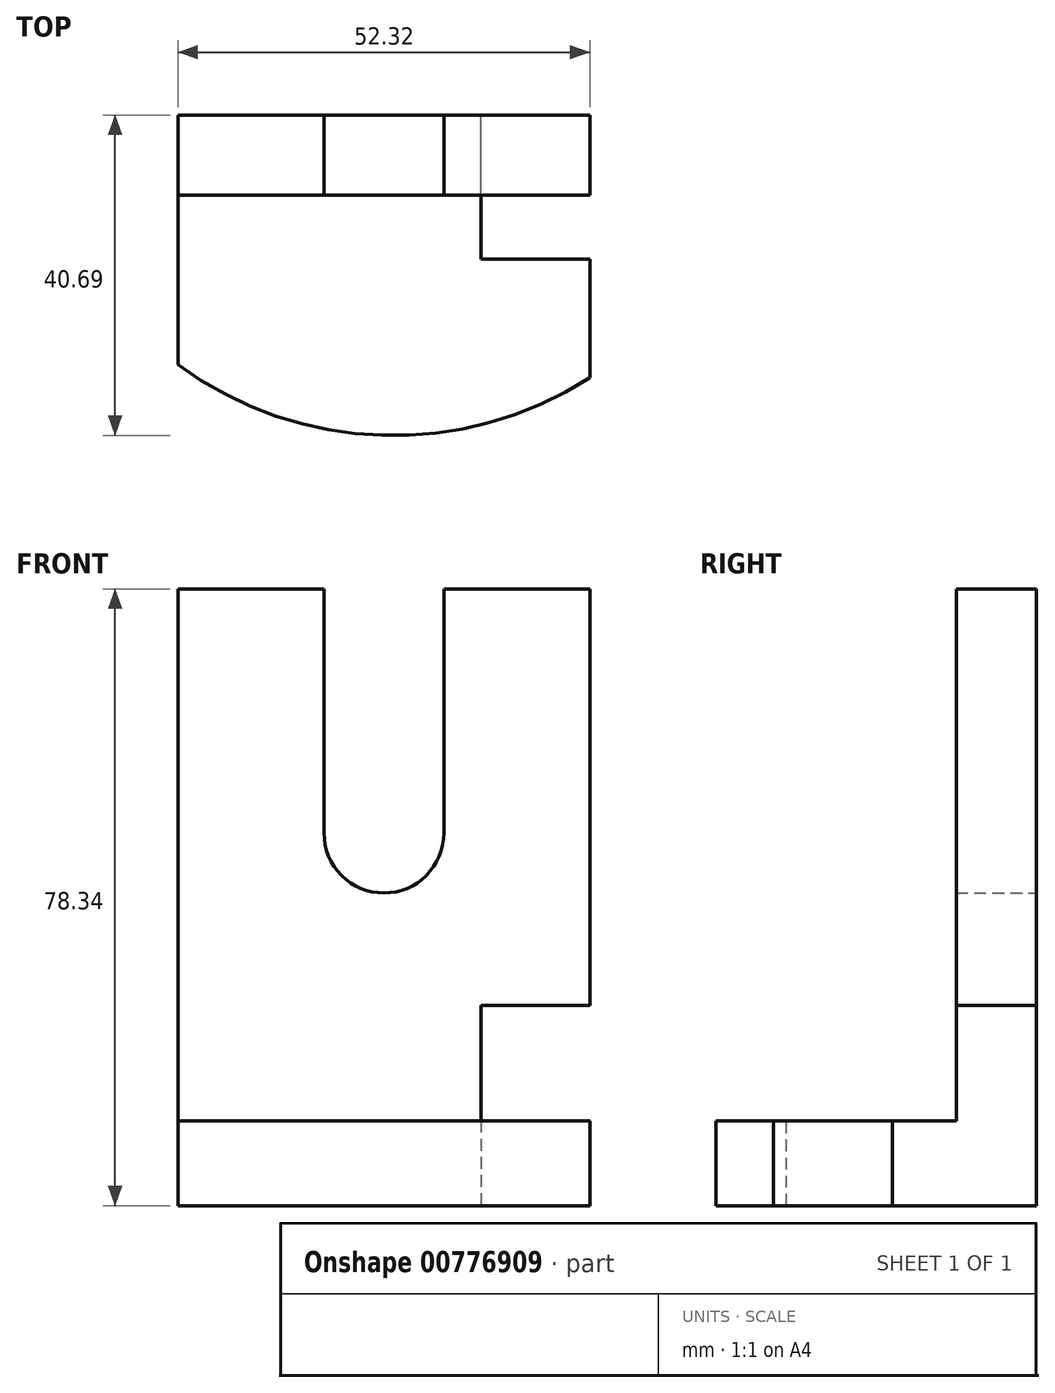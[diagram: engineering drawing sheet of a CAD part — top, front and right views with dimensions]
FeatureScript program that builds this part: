
annotation { "Feature Type Name" : "Feature", "Feature Type Description" : "" }
export const myFeature = defineFeature(function(context is Context, id is Id, definition is map)
    precondition{}
    {
        {
            var Q0;
            Q0=qCreatedBy(makeId("Front.planeOp"),FACE);
            var sketch = newSketch(context, id + "F0", { "sketchPlane" : qUnion([Q0])});
            skLineSegment(sketch, "E0.bottom", {"start": v(26.16, 39.17) * mm, "end": v(7.61, 39.17) * mm});
            skLineSegment(sketch, "E0.top", {"start": v(26.16, -39.17) * mm, "end": v(-26.16, -39.17) * mm});
            skLineSegment(sketch, "E0.left", {"start": v(26.16, 39.17) * mm, "end": v(26.16, -39.17) * mm});
            skLineSegment(sketch, "E0.right", {"start": v(-26.16, 39.17) * mm, "end": v(-26.16, -39.17) * mm});
            skPoint(sketch, "E0.middle", {"position": v(0, 0) * mm});
            skLineSegment(sketch, "E1.left", {"start": v(7.61, 39.17) * mm, "end": v(7.61, 8.16) * mm});
            skLineSegment(sketch, "E1.right", {"start": v(-7.61, 39.17) * mm, "end": v(-7.61, 8.16) * mm});
            skPoint(sketch, "E1.middle", {"position": v(0, 23.67) * mm});
            skLineSegment(sketch, "E2", {"start": v(-26.16, -28.38) * mm, "end": v(26.16, -28.38) * mm});
            skLineSegment(sketch, "E3.trimOffspring", {"start": v(-7.61, 39.17) * mm, "end": v(-26.16, 39.17) * mm});
            skArc(sketch, "E4", {"start": v(-7.61, 8.16) * mm, "mid": v(0, 0.55) * mm, "end": v(7.61, 8.16) * mm});
            skSolve(sketch);
        }
        {
            var Q0;
            {var subQ4=sQuery(id+"F0.wireOp",EDGE,"E0.bottom");Q0=makeQuery(id+"F0.imprint","IMPRINT",FACE,{"disambiguationData":[TD([[makeQuery(id+"F0.imprint","IMPRINT",EDGE,{"derivedFrom":subQ4}),1.0]])]});}
            extrude(context, id + "F1", {"entities" : qUnion([Q0]), "depth" : 10.16 * mm, "offsetDistance" : 25.4 * mm});
        }
        {
            var Q0;
            {var subQ0=sQuery(id+"F0.wireOp",EDGE,"E0.top");Q0=makeQuery(id+"F0.imprint","IMPRINT",FACE,{"disambiguationData":[TD([[makeQuery(id+"F0.imprint","IMPRINT",EDGE,{"derivedFrom":subQ0}),-1.0]])]});}
            extrude(context, id + "F2", {"entities" : qUnion([Q0]), "operationType" : NewBodyOperationType.ADD, "depth" : 45.2 * mm, "offsetDistance" : 25.4 * mm});
        }
        {
            var Q0;
            Q0=makeQuery(id+"F2.opExtrude","SWEPT_FACE",FACE,{"disambiguationData":[OSD([sQuery(id+"F0.wireOp",EDGE,"E2")])]});
            var sketch = newSketch(context, id + "F3", { "sketchPlane" : qUnion([Q0])});
            skArc(sketch, "E5", {"start": v(-26.16, -31.7) * mm, "mid": v(-0.26, -40.67) * mm, "end": v(26.16, -33.37) * mm});
            skSolve(sketch);
        }
        {
            var Q0;
            {var subQ0=sQuery(id+"F3.wireOp",EDGE,"E5");Q0=makeQuery(id+"F3.imprint","IMPRINT",FACE,{"disambiguationData":[TD([[makeQuery(id+"F3.imprint","IMPRINT",EDGE,{"derivedFrom":subQ0}),-1.0]])]});}
            extrude(context, id + "F4", {"entities" : qUnion([Q0]), "operationType" : NewBodyOperationType.REMOVE, "oppositeDirection" : true, "depth" : 25.4 * mm, "offsetDistance" : 25.4 * mm});
        }
        {
            var Q0;
            {var subQ4=sQuery(id+"F0.wireOp",EDGE,"E0.bottom");Q0=makeQuery(id+"F0.imprint","IMPRINT",FACE,{"disambiguationData":[TD([[makeQuery(id+"F0.imprint","IMPRINT",EDGE,{"derivedFrom":subQ4}),1.0]])]});}
            var sketch = newSketch(context, id + "F5", { "sketchPlane" : qUnion([Q0])});
            skLineSegment(sketch, "E6.bottom", {"start": v(26.72, -13.7) * mm, "end": v(12.32, -13.7) * mm});
            skLineSegment(sketch, "E6.top", {"start": v(26.72, -39.18) * mm, "end": v(12.32, -39.18) * mm});
            skLineSegment(sketch, "E6.left", {"start": v(26.72, -13.7) * mm, "end": v(26.72, -39.18) * mm});
            skLineSegment(sketch, "E6.right", {"start": v(12.32, -13.7) * mm, "end": v(12.32, -39.18) * mm});
            skSolve(sketch);
        }
        {
            var Q0;
            Q0 = qSketchRegion(id + "F5", true);
            extrude(context, id + "F6", {"entities" : qUnion([Q0]), "operationType" : NewBodyOperationType.REMOVE, "depth" : 18.29 * mm, "offsetDistance" : 25.4 * mm});
        }
    });
